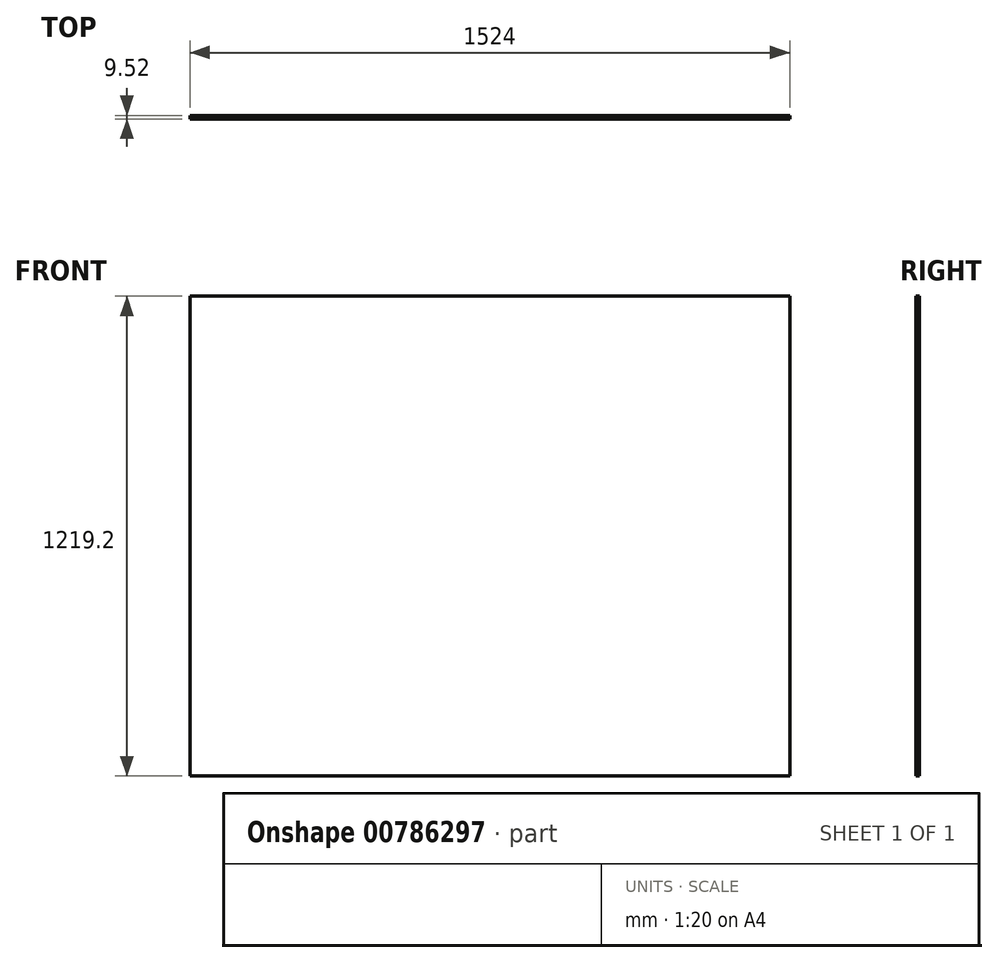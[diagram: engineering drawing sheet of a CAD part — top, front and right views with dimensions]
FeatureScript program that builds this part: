
annotation { "Feature Type Name" : "Feature", "Feature Type Description" : "" }
export const myFeature = defineFeature(function(context is Context, id is Id, definition is map)
    precondition{}
    {
        {
            var Q0;
            Q0=qCreatedBy(makeId("Front.planeOp"),FACE);
            var sketch = newSketch(context, id + "F0", { "sketchPlane" : qUnion([Q0])});
            skLineSegment(sketch, "E0.bottom", {"start": v(-762, 609.6) * mm, "end": v(762, 609.6) * mm});
            skLineSegment(sketch, "E0.top", {"start": v(-762, -609.6) * mm, "end": v(762, -609.6) * mm});
            skLineSegment(sketch, "E0.left", {"start": v(-762, 609.6) * mm, "end": v(-762, -609.6) * mm});
            skLineSegment(sketch, "E0.right", {"start": v(762, 609.6) * mm, "end": v(762, -609.6) * mm});
            skPoint(sketch, "E0.middle", {"position": v(0, 0) * mm});
            skSolve(sketch);
        }
        {
            var Q0;
            Q0=makeQuery(id+"F0.imprint","IMPRINT",FACE,{"disambiguationData":[TD([[makeQuery(id+"F0.imprint","IMPRINT",EDGE,{"derivedFrom":sQuery(id+"F0.wireOp",EDGE,"E0.bottom")}),-1.0]])]});
            extrude(context, id + "F1", {"entities" : qUnion([Q0]), "endBound" : BoundingType.SYMMETRIC, "depth" : 9.52 * mm, "offsetDistance" : 25.4 * mm});
        }
    });
